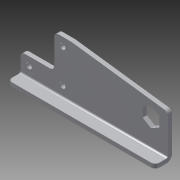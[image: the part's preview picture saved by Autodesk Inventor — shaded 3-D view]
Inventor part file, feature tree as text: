
AUTODESK INVENTOR PART (.ipt)
format: ipt  version: 2014 (Build 180170000, 170)  size: 178,688 bytes
history: native  units: in
note: dims shown in document units (in); Inventor stores cm internally (conversion verified against a paired STEP export)
features: sheet_metal_op x4, other x3, sketch x2, fillet x1
ambient origin geometry x8: Origin, YZ Plane, XZ Plane, XY Plane, X Axis, Y Axis, Z Axis, Center Point
bodies: Solid1 (feature_tree)
feature tree (10):
  sheet_metal_op  "Face1"
  sheet_metal_op  "Flange1"
  fillet  "Fillet2"  Radius=0.5in
  sketch  "Sketch1"  dims[d1=1.0in]
  other  "Plate1"
  sketch  "Sketch2"  dims[d2=1.0in d3=0.5in d4=4.375in d5=0.5in d6=0.75in d7=0.5in d8=90.0deg d9=1.125in d10=0.163in d11=0.25in d12=0.25in d13=0.7874in d15=1.0in d16=0.3937in d18=1.0in d20=0.7874in d22=1.0in d23=0.3937in d25=1.0in d27=0.125in d29=0.125in d30=0.0625in d31=0.25in d32=0.125in d33=0.5in d34=90.0deg d35=0.05in d36=0.5in d37=0.125in d38=0.125in d39=0.125in]
  other  "Plate2"
  sheet_metal_op  "Bend1"
  sheet_metal_op  "Corner1"
  other  "Definition1"
